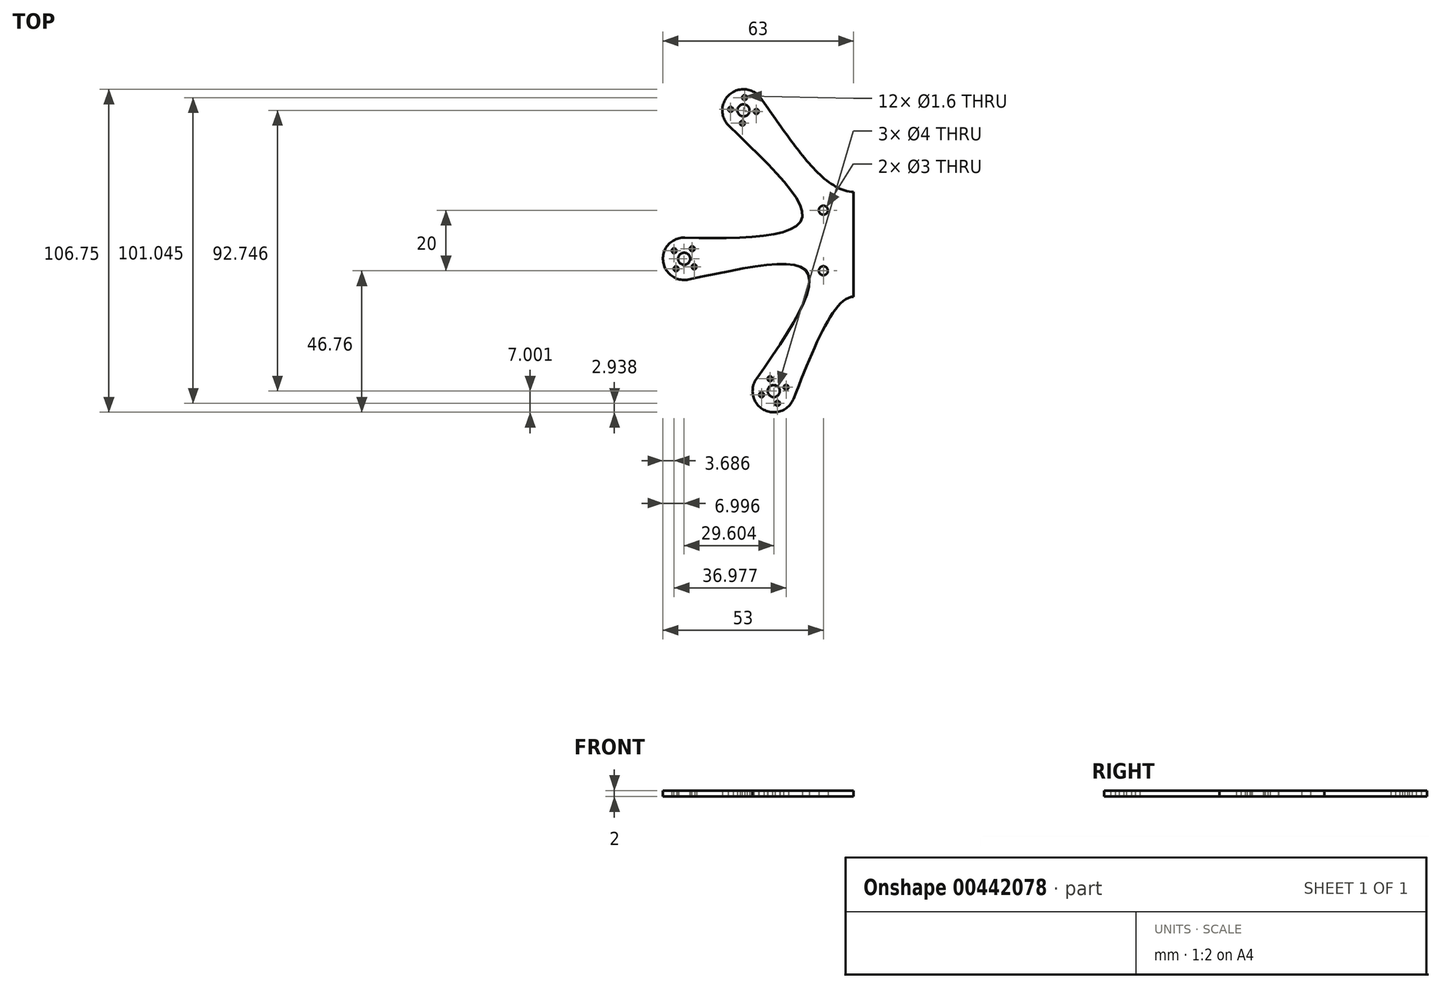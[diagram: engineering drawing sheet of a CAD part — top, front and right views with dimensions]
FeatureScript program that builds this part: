
annotation { "Feature Type Name" : "Feature", "Feature Type Description" : "" }
export const myFeature = defineFeature(function(context is Context, id is Id, definition is map)
    precondition{}
    {
        {
            var Q0;
            Q0=qCreatedBy(makeId("Top.planeOp"),FACE);
            var sketch = newSketch(context, id + "F0", { "sketchPlane" : qUnion([Q0])});
            skLineSegment(sketch, "E0", {"start": v(0, 0) * mm, "end": v(-36.4, 42.99) * mm, "construction": true});
            skCircle(sketch, "E1", {"center": v(-36.4, 42.99) * mm, "radius": 25.4 * mm, "construction": true});
            skLineSegment(sketch, "E2.bottom", {"start": v(13.5, 13.5) * mm, "end": v(-13.5, 13.5) * mm, "construction": true});
            skLineSegment(sketch, "E2.top", {"start": v(13.5, -13.5) * mm, "end": v(-13.5, -13.5) * mm, "construction": true});
            skLineSegment(sketch, "E2.left", {"start": v(13.5, 13.5) * mm, "end": v(13.5, -13.5) * mm, "construction": true});
            skLineSegment(sketch, "E2.right", {"start": v(-13.5, 13.5) * mm, "end": v(-13.5, -13.5) * mm, "construction": true});
            skPoint(sketch, "E2.middle", {"position": v(0, 0) * mm});
            skLineSegment(sketch, "E3", {"start": v(0, 0) * mm, "end": v(-56, -6.04) * mm, "construction": true});
            skCircle(sketch, "E4", {"center": v(-56, -6.04) * mm, "radius": 25.4 * mm, "construction": true});
            skLineSegment(sketch, "E5", {"start": v(0, 0) * mm, "end": v(-26.4, -49.76) * mm, "construction": true});
            skCircle(sketch, "E6", {"center": v(-26.4, -49.76) * mm, "radius": 25.4 * mm, "construction": true});
            skArc(sketch, "E7", {"start": v(-30.71, 47.07) * mm, "mid": v(-40.96, 48.3) * mm, "end": v(-41.3, 37.98) * mm});
            skArc(sketch, "E8", {"start": v(-55.83, 0.96) * mm, "mid": v(-62.98, -6.66) * mm, "end": v(-54.6, -12.9) * mm});
            skArc(sketch, "E9", {"start": v(-32.11, -45.71) * mm, "mid": v(-29.74, -55.91) * mm, "end": v(-19.9, -52.34) * mm});
            skLineSegment(sketch, "E10", {"start": v(-13.59, 16.05) * mm, "end": v(-17.78, 12.5) * mm, "construction": true});
            skLineSegment(sketch, "E11", {"start": v(-17.78, 12.5) * mm, "end": v(-29.42, 26.23) * mm, "construction": true});
            skLineSegment(sketch, "E12", {"start": v(-29.42, 26.23) * mm, "end": v(-21.02, 33.34) * mm, "construction": true});
            skLineSegment(sketch, "E13", {"start": v(-21.02, 33.34) * mm, "end": v(-9.4, 19.6) * mm, "construction": true});
            skLineSegment(sketch, "E14", {"start": v(-9.4, 19.6) * mm, "end": v(-13.59, 16.05) * mm, "construction": true});
            skCircle(sketch, "E15", {"center": v(0, 0) * mm, "radius": 21.03 * mm, "construction": true});
            skLineSegment(sketch, "E16", {"start": v(-13.59, 16.05) * mm, "end": v(-20.9, -2.25) * mm, "construction": true});
            skLineSegment(sketch, "E17", {"start": v(-20.9, -2.25) * mm, "end": v(-9.85, -18.57) * mm, "construction": true});
            skLineSegment(sketch, "E18", {"start": v(-9.85, -18.57) * mm, "end": v(9.85, -18.57) * mm, "construction": true});
            skLineSegment(sketch, "E19.MirrorCS", {"start": v(0, 0) * mm, "end": v(26.4, -49.76) * mm, "construction": true});
            skFitSpline(sketch, "E20", {"points": [v(-41.3, 37.98) * mm, v(-17.25, 6.9) * mm, v(-55.83, 0.96) * mm], "startDerivative": vector(77.88, -76.1) * mm, "endDerivative": vector(-107.25, 2.68) * mm});
            skFitSpline(sketch, "E21", {"points": [v(-54.6, -12.9) * mm, v(-15.38, -10.41) * mm, v(-32.11, -45.71) * mm], "startDerivative": vector(107.6, 21.98) * mm, "endDerivative": vector(-61.9, -87.45) * mm});
            skCircle(sketch, "E22.MirrorC", {"center": v(26.4, -49.76) * mm, "radius": 7 * mm});
            skFitSpline(sketch, "E23", {"points": [v(-19.9, -52.34) * mm, v(0, -18.57) * mm, v(19.88, -52.31) * mm], "startDerivative": vector(40.16, 101.2) * mm, "endDerivative": vector(39.45, -100.76) * mm});
            skLineSegment(sketch, "E24", {"start": v(-13.59, 16.05) * mm, "end": v(13.59, 16.05) * mm, "construction": true});
            skLineSegment(sketch, "E25.MirrorCS", {"start": v(0, 0) * mm, "end": v(36.4, 42.99) * mm, "construction": true});
            skCircle(sketch, "E26.MirrorC", {"center": v(36.4, 42.99) * mm, "radius": 7 * mm});
            skFitSpline(sketch, "E27", {"points": [v(-30.71, 47.07) * mm, v(0, 16.05) * mm, v(30.35, 46.51) * mm], "startDerivative": vector(62.03, -86.4) * mm, "endDerivative": vector(53.6, 91.96) * mm});
            skLineSegment(sketch, "E28", {"start": v(0, 16.05) * mm, "end": v(0, 31.28) * mm, "construction": true});
            skLineSegment(sketch, "E29.bottom", {"start": v(9.5, 21.28) * mm, "end": v(-9.5, 21.28) * mm, "construction": true});
            skLineSegment(sketch, "E29.top", {"start": v(9.5, 41.28) * mm, "end": v(-9.5, 41.28) * mm, "construction": true});
            skLineSegment(sketch, "E29.left", {"start": v(9.5, 21.28) * mm, "end": v(9.5, 41.28) * mm, "construction": true});
            skLineSegment(sketch, "E29.right", {"start": v(-9.5, 21.28) * mm, "end": v(-9.5, 41.28) * mm, "construction": true});
            skPoint(sketch, "E29.middle", {"position": v(0, 31.28) * mm});
            skLineSegment(sketch, "E30", {"start": v(-11.68, 29.42) * mm, "end": v(-9.82, 38.86) * mm});
            skLineSegment(sketch, "E31", {"start": v(-6.88, 41.28) * mm, "end": v(0, 41.28) * mm});
            skPoint(sketch, "E32.visualSharp", {"position": v(-9.34, 41.28) * mm});
            skArc(sketch, "E32.filletArc", {"start": v(-6.88, 41.28) * mm, "mid": v(-8.78, 40.6) * mm, "end": v(-9.82, 38.86) * mm});
            skPoint(sketch, "E33.newPointB", {"position": v(-12.13, 27.14) * mm});
            skArc(sketch, "E33.filletArc", {"start": v(-16.96, 28.11) * mm, "mid": v(-13.9, 27.1) * mm, "end": v(-11.68, 29.42) * mm});
            skLineSegment(sketch, "E34", {"start": v(0, 41.28) * mm, "end": v(0, -18.57) * mm});
            skCircle(sketch, "E35", {"center": v(-36.4, 42.99) * mm, "radius": 2 * mm});
            skCircle(sketch, "E36", {"center": v(-56, -6.04) * mm, "radius": 2 * mm});
            skCircle(sketch, "E37", {"center": v(-26.4, -49.76) * mm, "radius": 2 * mm});
            skLineSegment(sketch, "E38", {"start": v(-36.4, 42.99) * mm, "end": v(-32.16, 42.64) * mm, "construction": true});
            skCircle(sketch, "E39", {"center": v(-32.16, 42.64) * mm, "radius": 0.8 * mm});
            skCircle(sketch, "E40.1.0", {"center": v(-36.05, 47.22) * mm, "radius": 0.8 * mm});
            skCircle(sketch, "E40.2.0", {"center": v(-40.64, 43.34) * mm, "radius": 0.8 * mm});
            skCircle(sketch, "E40.3.0", {"center": v(-36.75, 38.75) * mm, "radius": 0.8 * mm});
            skLineSegment(sketch, "E41", {"start": v(-56, -6.04) * mm, "end": v(-53.34, -2.73) * mm, "construction": true});
            skCircle(sketch, "E42", {"center": v(-53.34, -2.73) * mm, "radius": 0.8 * mm});
            skCircle(sketch, "E43.1.0", {"center": v(-59.31, -3.37) * mm, "radius": 0.8 * mm});
            skCircle(sketch, "E43.2.0", {"center": v(-58.67, -9.35) * mm, "radius": 0.8 * mm});
            skCircle(sketch, "E43.3.0", {"center": v(-52.7, -8.7) * mm, "radius": 0.8 * mm});
            skLineSegment(sketch, "E44", {"start": v(-26.4, -49.76) * mm, "end": v(-27.65, -45.7) * mm, "construction": true});
            skCircle(sketch, "E45", {"center": v(-27.65, -45.7) * mm, "radius": 0.8 * mm});
            skCircle(sketch, "E46.1.0", {"center": v(-30.46, -51) * mm, "radius": 0.8 * mm});
            skCircle(sketch, "E46.2.0", {"center": v(-25.15, -53.82) * mm, "radius": 0.8 * mm});
            skCircle(sketch, "E46.3.0", {"center": v(-22.34, -48.51) * mm, "radius": 0.8 * mm});
            skCircle(sketch, "E47", {"center": v(-10, 10) * mm, "radius": 1.5 * mm});
            skCircle(sketch, "E48.0.1.0", {"center": v(-10, -10) * mm, "radius": 1.5 * mm});
            skCircle(sketch, "E48.1.0.0", {"center": v(10, 10) * mm, "radius": 1.5 * mm});
            skCircle(sketch, "E48.1.1.0", {"center": v(10, -10) * mm, "radius": 1.5 * mm});
            skLineSegment(sketch, "E48.direction1", {"start": v(-10, 10) * mm, "end": v(10, 10) * mm, "construction": true});
            skLineSegment(sketch, "E48.direction2", {"start": v(-10, 10) * mm, "end": v(-10, -10) * mm, "construction": true});
            skSolve(sketch);
        }
        {
            var Q0;
            Q0=makeQuery(id+"F0.imprint","IMPRINT",FACE,{"disambiguationData":[TD([[makeQuery(id+"F0.imprint","IMPRINT",EDGE,{"derivedFrom":sQuery(id+"F0.wireOp",EDGE,"E7")}),1.0]])]});
            extrude(context, id + "F1", {"entities" : qUnion([Q0]), "depth" : 2 * mm});
        }
    });
